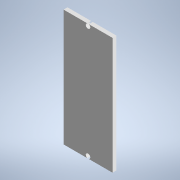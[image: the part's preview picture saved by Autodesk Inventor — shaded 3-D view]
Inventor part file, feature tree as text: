
AUTODESK INVENTOR PART (.ipt)
format: ipt  version: 2022 (Build 260153000, 153)  size: 103,424 bytes
history: native  units: mm
features: reference x6, other x4, extrude x1, sketch x1
ambient origin geometry x8: Origin, YZ Plane, XZ Plane, XY Plane, X Axis, Y Axis, Z Axis, Center Point
bodies: Body1 (feature_tree)
feature tree (12):
  other  "Твердое тело1"
  extrude  "Выдавливание1"  Depth=0.3mm
  sketch  "Эскиз1"
  reference  "Ссылка1"
  reference  "Ссылка2"
  reference  "Ссылка3"
  reference  "Ссылка4"
  reference  "Ссылка5"
  reference  "Ссылка6"
  other  "<path> - Robot.iam"
  other  "000.000 - Robot.iam"
  other  "battery_case:1"
note: 1 file-system path scrubbed to <path> (originals preserved in map.json)
